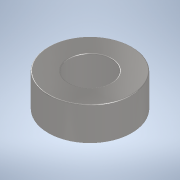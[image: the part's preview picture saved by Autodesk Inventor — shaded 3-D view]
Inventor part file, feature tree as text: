
AUTODESK INVENTOR PART (.ipt)
format: ipt  version: 2022 (Build 260153000, 153)  size: 133,632 bytes
history: native  units: in
note: dims shown in document units (in); Inventor stores cm internally (conversion verified against a paired STEP export)
features: extrude x1, fillet x1, sketch x1
ambient origin geometry x8: Origin, YZ Plane, XZ Plane, XY Plane, X Axis, Y Axis, Z Axis, Center Point
bodies: Solid1 (feature_tree)
feature tree (3):
  extrude  "Extrusion1"  Depth=0.3937in
  fillet  "Fillet1"  Radius=0.1575in
  sketch  "Sketch1"  dims[d0=0.1969in d1=0.3937in d2=0.1575in d3=0.0in d4=0.0039in]
